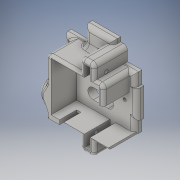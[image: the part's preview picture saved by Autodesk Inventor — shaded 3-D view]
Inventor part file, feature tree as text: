
AUTODESK INVENTOR PART (.ipt)
format: ipt  version: 2016 (Build 200138000, 138)  size: 567,808 bytes
history: native  units: in
note: dims shown in document units (in); Inventor stores cm internally (conversion verified against a paired STEP export)
features: sketch x16, other x3
ambient origin geometry x8: Origin, YZ Plane, XZ Plane, XY Plane, X Axis, Y Axis, Z Axis, Center Point
bodies: Solid1 (feature_tree)
feature tree (19):
  other  "Hip_holder_v2.ipt"
  other  "Solid1::Hip_holder_v2.ipt"
  other  "TaggingFeature1"
  sketch  "Sketch1"  dims[d0=0.3937in]
  sketch  "Sketch12"
  sketch  "Sketch14"
  sketch  "Sketch17"
  sketch  "Sketch18"
  sketch  "Sketch21"
  sketch  "Sketch22"
  sketch  "Sketch23"
  sketch  "Sketch24"
  sketch  "Sketch25"
  sketch  "Sketch26"
  sketch  "Sketch27"
  sketch  "Sketch28"
  sketch  "Sketch29"
  sketch  "Sketch30"
  sketch  "Sketch31"
